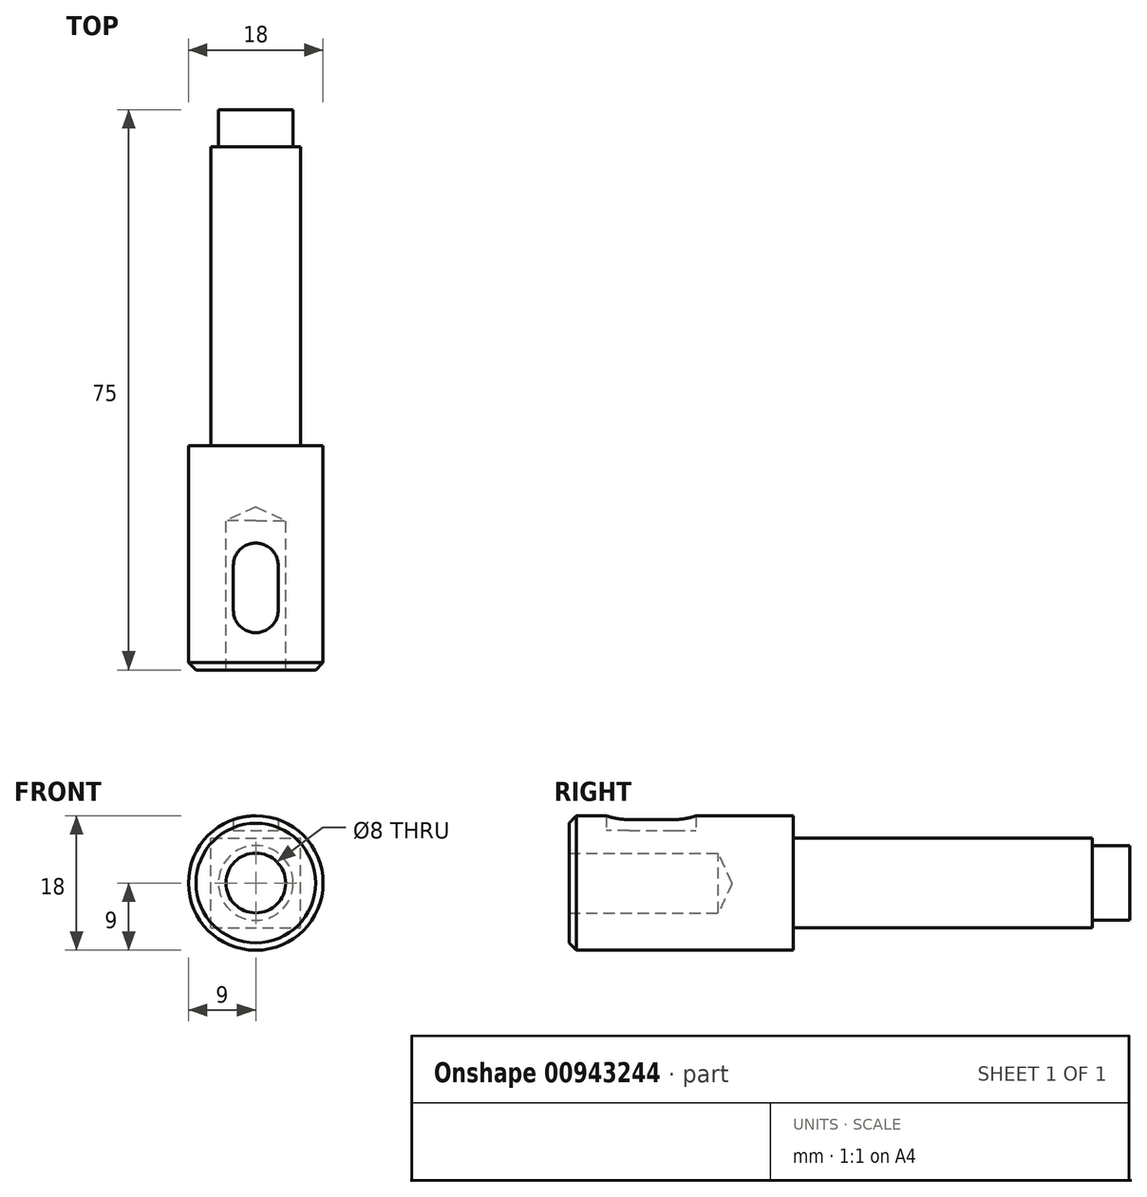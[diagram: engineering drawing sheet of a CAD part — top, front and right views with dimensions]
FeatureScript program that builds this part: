
annotation { "Feature Type Name" : "Feature", "Feature Type Description" : "" }
export const myFeature = defineFeature(function(context is Context, id is Id, definition is map)
    precondition{}
    {
        {
            var Q0;
            Q0=qCreatedBy(makeId("Top.planeOp"),FACE);
            var sketch = newSketch(context, id + "F0", { "sketchPlane" : qUnion([Q0])});
            skLineSegment(sketch, "E0", {"start": v(0, 53.17) * mm, "end": v(5, 53.17) * mm});
            skLineSegment(sketch, "E1", {"start": v(5, 53.17) * mm, "end": v(5, 48.17) * mm});
            skLineSegment(sketch, "E2", {"start": v(5, 48.17) * mm, "end": v(6, 48.17) * mm});
            skLineSegment(sketch, "E3", {"start": v(6, 48.17) * mm, "end": v(6, 8.17) * mm});
            skLineSegment(sketch, "E4", {"start": v(6, 8.17) * mm, "end": v(9, 8.17) * mm});
            skLineSegment(sketch, "E5", {"start": v(9, 8.17) * mm, "end": v(9, -20.83) * mm});
            skLineSegment(sketch, "E6", {"start": v(9, -20.83) * mm, "end": v(8, -21.83) * mm});
            skLineSegment(sketch, "E7", {"start": v(8, -21.83) * mm, "end": v(4, -21.83) * mm});
            skLineSegment(sketch, "E8", {"start": v(4, -21.83) * mm, "end": v(4, -6.83) * mm});
            skLineSegment(sketch, "E9", {"start": v(4, -6.83) * mm, "end": v(4, -1.83) * mm});
            skLineSegment(sketch, "E10", {"start": v(4, -1.83) * mm, "end": v(0, 0) * mm});
            skLineSegment(sketch, "E11", {"start": v(0, 53.17) * mm, "end": v(0, 0) * mm});
            skSolve(sketch);
        }
        {
            var Q0;
            Q0=makeQuery(id+"F0.imprint","IMPRINT",FACE,{"disambiguationData":[TD([[makeQuery(id+"F0.imprint","IMPRINT",EDGE,{"derivedFrom":sQuery(id+"F0.wireOp",EDGE,"E0")}),-1.0]])]});
            var Q1;
            Q1=sQuery(id+"F0.wireOp",EDGE,"E11");
            revolve(context, id + "F1", {"surfaceOperationType" : NewSurfaceOperationType.NEW, "entities" : qUnion([Q0]), "axis" : qUnion([Q1]), "revolveType" : RevolveType.FULL});
        }
        {
            var Q0;
            Q0=qCreatedBy(makeId("Top.planeOp"),FACE);
            cPlane(context, id + "F2", {"entities" : qUnion([Q0]), "cplaneType" : CPlaneType.OFFSET, "offset" : 7 * mm, "width" : 150 * mm, "height" : 150 * mm});
        }
        {
            var Q0;
            Q0=qCreatedBy(id+"F2.planeOp",FACE);
            var sketch = newSketch(context, id + "F3", { "sketchPlane" : qUnion([Q0])});
            skLineSegment(sketch, "E12", {"start": v(0, -13.83) * mm, "end": v(0, -7.83) * mm});
            skArc(sketch, "E13.0.startCap", {"start": v(3, -13.83) * mm, "mid": v(0, -16.83) * mm, "end": v(-3, -13.83) * mm});
            skArc(sketch, "E13.0.endCap", {"start": v(-3, -7.83) * mm, "mid": v(0, -4.83) * mm, "end": v(3, -7.83) * mm});
            skLineSegment(sketch, "E13.0.left", {"start": v(-3, -13.83) * mm, "end": v(-3, -7.83) * mm});
            skLineSegment(sketch, "E13.0.right", {"start": v(3, -13.83) * mm, "end": v(3, -7.83) * mm});
            skSolve(sketch);
        }
        {
            var Q0;
            Q0=qSketchRegion(id+"F3",true);
            extrude(context, id + "F4", {"entities" : qUnion([Q0]), "operationType" : NewBodyOperationType.REMOVE, "depth" : 25 * mm, "offsetDistance" : 25 * mm});
        }
        {
            var Q0;
            Q0=makeQuery(id+"F1.opRevolve","SWEPT_FACE",FACE,{"disambiguationData":[OSD([sQuery(id+"F0.wireOp",EDGE,"E2")])]});
            var sketch = newSketch(context, id + "F5", { "sketchPlane" : qUnion([Q0])});
            skLineSegment(sketch, "E14.bottom", {"start": v(-6, 6) * mm, "end": v(6, 6) * mm});
            skLineSegment(sketch, "E14.top", {"start": v(-6, -6) * mm, "end": v(6, -6) * mm});
            skLineSegment(sketch, "E14.left", {"start": v(-6, 6) * mm, "end": v(-6, -6) * mm});
            skLineSegment(sketch, "E14.right", {"start": v(6, 6) * mm, "end": v(6, -6) * mm});
            skPoint(sketch, "E14.middle", {"position": v(0, 0) * mm});
            skSolve(sketch);
        }
        {
            var Q0;
            {var subQ0=sQuery(id+"F5.wireOp",EDGE,"E14.left");var subQ1=sQuery(id+"F5.wireOp",EDGE,"E14.bottom");var subQ2=makeQuery(id+"F5.imprint","INTERSECT",VERTEX,{"derivedFrom":[subQ1,subQ0]});Q0=makeQuery(id+"F5.imprint","IMPRINT",FACE,{"disambiguationData":[TD([[makeQuery(id+"F5.imprint","IMPRINT",EDGE,{"disambiguationData":[TD([[subQ2,-1.0]])],"derivedFrom":subQ1}),-1.0]])]});}
            var Q1;
            {var subQ0=sQuery(id+"F5.wireOp",EDGE,"E14.left");var subQ1=sQuery(id+"F5.wireOp",EDGE,"E14.top");var subQ2=makeQuery(id+"F5.imprint","INTERSECT",VERTEX,{"derivedFrom":[subQ1,subQ0]});Q1=makeQuery(id+"F5.imprint","IMPRINT",FACE,{"disambiguationData":[TD([[makeQuery(id+"F5.imprint","IMPRINT",EDGE,{"disambiguationData":[TD([[subQ2,-1.0]])],"derivedFrom":subQ1}),1.0]])]});}
            var Q2;
            {var subQ0=sQuery(id+"F5.wireOp",EDGE,"E14.right");var subQ1=sQuery(id+"F5.wireOp",EDGE,"E14.top");var subQ2=makeQuery(id+"F5.imprint","INTERSECT",VERTEX,{"derivedFrom":[subQ1,subQ0]});Q2=makeQuery(id+"F5.imprint","IMPRINT",FACE,{"disambiguationData":[TD([[makeQuery(id+"F5.imprint","IMPRINT",EDGE,{"disambiguationData":[TD([[subQ2,1.0]])],"derivedFrom":subQ1}),1.0]])]});}
            var Q3;
            {var subQ0=sQuery(id+"F5.wireOp",EDGE,"E14.right");var subQ1=sQuery(id+"F5.wireOp",EDGE,"E14.bottom");var subQ2=makeQuery(id+"F5.imprint","INTERSECT",VERTEX,{"derivedFrom":[subQ1,subQ0]});Q3=makeQuery(id+"F5.imprint","IMPRINT",FACE,{"disambiguationData":[TD([[makeQuery(id+"F5.imprint","IMPRINT",EDGE,{"disambiguationData":[TD([[subQ2,1.0]])],"derivedFrom":subQ1}),-1.0]])]});}
            extrude(context, id + "F6", {"entities" : qUnion([Q0, Q1, Q2, Q3]), "operationType" : NewBodyOperationType.ADD, "endBound" : BoundingType.UP_TO_NEXT, "oppositeDirection" : true, "depth" : 25 * mm, "offsetDistance" : 25 * mm});
        }
    });
